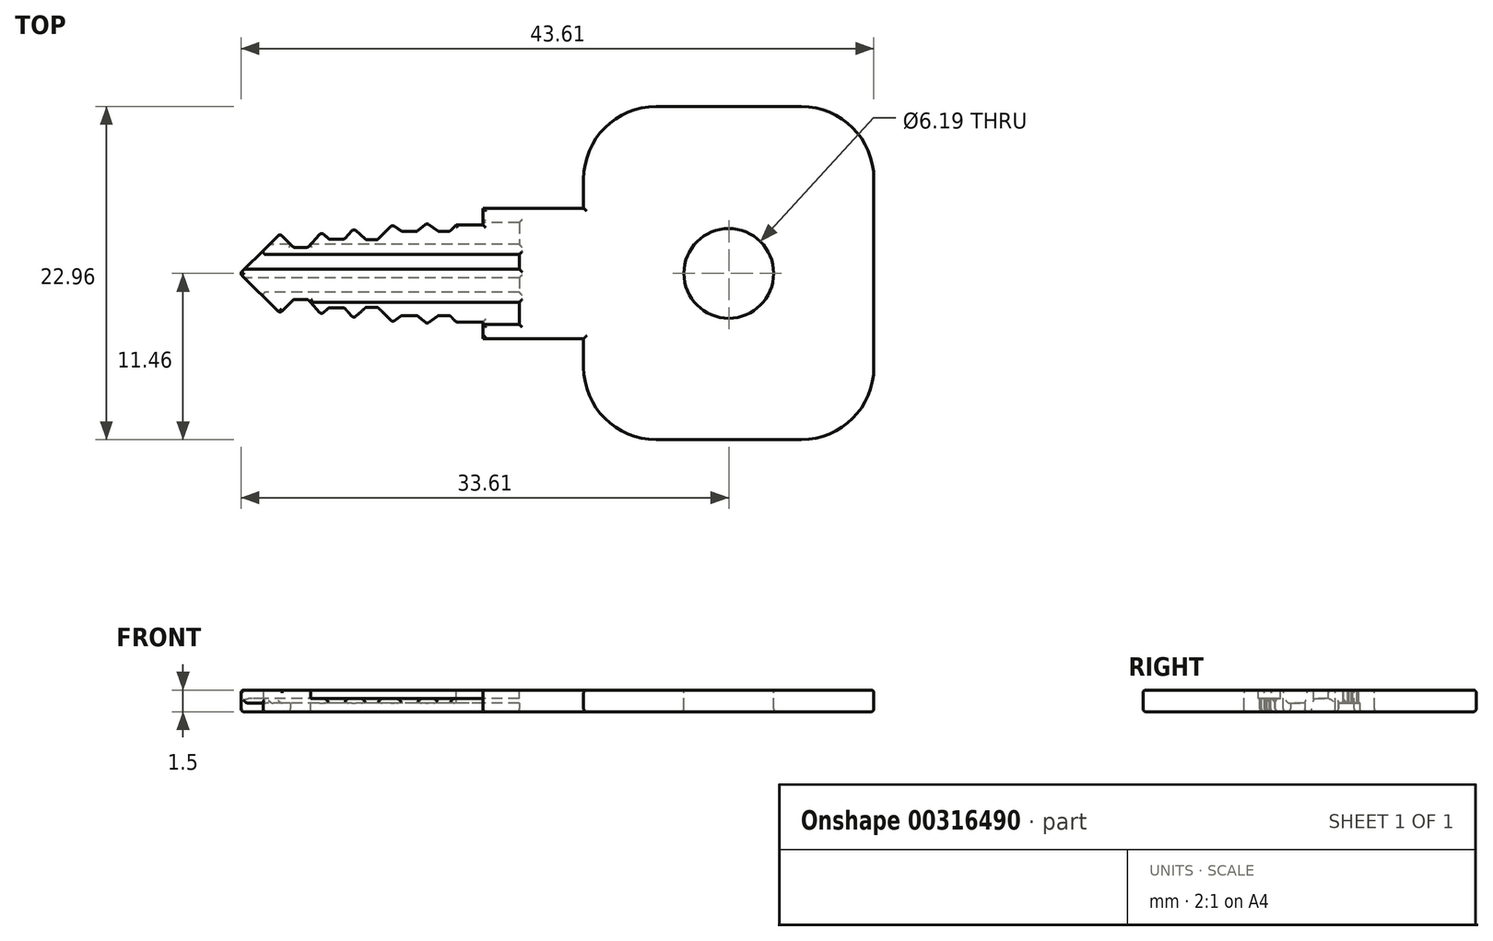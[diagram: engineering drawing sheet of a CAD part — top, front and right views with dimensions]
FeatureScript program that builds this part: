
annotation { "Feature Type Name" : "Feature", "Feature Type Description" : "" }
export const myFeature = defineFeature(function(context is Context, id is Id, definition is map)
    precondition{}
    {
        {
            var Q0;
            Q0=qCreatedBy(makeId("Right.planeOp"),FACE);
            var sketch = newSketch(context, id + "F0", { "sketchPlane" : qUnion([Q0])});
            skLineSegment(sketch, "E0.bottom", {"start": v(4.5, 0.75) * mm, "end": v(-4.5, 0.75) * mm});
            skLineSegment(sketch, "E0.top", {"start": v(4.5, -0.75) * mm, "end": v(-4.5, -0.75) * mm});
            skLineSegment(sketch, "E0.left", {"start": v(4.5, 0.75) * mm, "end": v(4.5, -0.75) * mm});
            skLineSegment(sketch, "E0.right", {"start": v(-4.5, 0.75) * mm, "end": v(-4.5, -0.75) * mm});
            skPoint(sketch, "E0.middle", {"position": v(0, 0) * mm});
            skSolve(sketch);
        }
        {
            var Q0;
            Q0 = qSketchRegion(id + "F0", true);
            extrude(context, id + "F1", {"entities" : qUnion([Q0]), "depth" : 25 * mm});
        }
        {
            var Q0;
            Q0=makeQuery(id+"F1.opExtrude","SWEPT_FACE",FACE,{"disambiguationData":[OSD([sQuery(id+"F0.wireOp",EDGE,"E0.bottom")])]});
            var sketch = newSketch(context, id + "F2", { "sketchPlane" : qUnion([Q0])});
            skLineSegment(sketch, "E1", {"start": v(0, 0) * mm, "end": v(0, -4.5) * mm});
            skLineSegment(sketch, "E2", {"start": v(18.06, -4.5) * mm, "end": v(18.06, -3.35) * mm});
            skLineSegment(sketch, "E3", {"start": v(18.06, -3.35) * mm, "end": v(16.22, -3.35) * mm});
            skLineSegment(sketch, "E4", {"start": v(16.22, -3.35) * mm, "end": v(15.77, -2.9) * mm});
            skLineSegment(sketch, "E5", {"start": v(15.77, -2.9) * mm, "end": v(14.99, -2.9) * mm});
            skLineSegment(sketch, "E6", {"start": v(14.99, -2.9) * mm, "end": v(14.2, -3.47) * mm});
            skLineSegment(sketch, "E7", {"start": v(14.2, -3.47) * mm, "end": v(13.51, -2.9) * mm});
            skLineSegment(sketch, "E8", {"start": v(13.51, -2.9) * mm, "end": v(12.47, -2.9) * mm});
            skLineSegment(sketch, "E9", {"start": v(12.47, -2.9) * mm, "end": v(11.83, -3.35) * mm});
            skLineSegment(sketch, "E10", {"start": v(11.83, -3.35) * mm, "end": v(10.8, -2.33) * mm});
            skLineSegment(sketch, "E11", {"start": v(10.8, -2.33) * mm, "end": v(10, -2.33) * mm});
            skLineSegment(sketch, "E12", {"start": v(10, -2.33) * mm, "end": v(9.16, -3.1) * mm});
            skLineSegment(sketch, "E13", {"start": v(9.16, -3.1) * mm, "end": v(8.5, -2.36) * mm});
            skLineSegment(sketch, "E14", {"start": v(8.5, -2.36) * mm, "end": v(7.45, -2.36) * mm});
            skLineSegment(sketch, "E15", {"start": v(7.45, -2.36) * mm, "end": v(6.93, -2.83) * mm});
            skLineSegment(sketch, "E16", {"start": v(6.93, -2.83) * mm, "end": v(6, -1.8) * mm});
            skLineSegment(sketch, "E17", {"start": v(6, -1.8) * mm, "end": v(5, -1.8) * mm});
            skLineSegment(sketch, "E18", {"start": v(5, -1.8) * mm, "end": v(4.07, -2.73) * mm});
            skLineSegment(sketch, "E19", {"start": v(4.07, -2.73) * mm, "end": v(1.3, 0) * mm});
            skLineSegment(sketch, "E20", {"start": v(1.3, 0) * mm, "end": v(0, 0) * mm});
            skLineSegment(sketch, "E21.MirrorCS", {"start": v(14.2, 3.47) * mm, "end": v(13.51, 2.9) * mm});
            skLineSegment(sketch, "E22.MirrorCS", {"start": v(10.8, 2.33) * mm, "end": v(10, 2.33) * mm});
            skLineSegment(sketch, "E23.MirrorCS", {"start": v(16.22, 3.35) * mm, "end": v(15.77, 2.9) * mm});
            skLineSegment(sketch, "E24.MirrorCS", {"start": v(15.77, 2.9) * mm, "end": v(14.99, 2.9) * mm});
            skLineSegment(sketch, "E25.MirrorCS", {"start": v(7.45, 2.36) * mm, "end": v(6.93, 2.83) * mm});
            skLineSegment(sketch, "E26.MirrorCS", {"start": v(12.47, 2.9) * mm, "end": v(11.83, 3.35) * mm});
            skLineSegment(sketch, "E27.MirrorCS", {"start": v(14.99, 2.9) * mm, "end": v(14.2, 3.47) * mm});
            skLineSegment(sketch, "E28.MirrorCS", {"start": v(0, 0) * mm, "end": v(0, 4.5) * mm});
            skLineSegment(sketch, "E29.MirrorCS", {"start": v(18.06, 4.5) * mm, "end": v(18.06, 3.35) * mm});
            skLineSegment(sketch, "E30.MirrorCS", {"start": v(6, 1.8) * mm, "end": v(5, 1.8) * mm});
            skLineSegment(sketch, "E31.MirrorCS", {"start": v(18.06, 3.35) * mm, "end": v(16.22, 3.35) * mm});
            skLineSegment(sketch, "E32.MirrorCS", {"start": v(9.16, 3.1) * mm, "end": v(8.5, 2.36) * mm});
            skLineSegment(sketch, "E33.MirrorCS", {"start": v(5, 1.8) * mm, "end": v(4.07, 2.73) * mm});
            skLineSegment(sketch, "E34.MirrorCS", {"start": v(13.51, 2.9) * mm, "end": v(12.47, 2.9) * mm});
            skLineSegment(sketch, "E35.MirrorCS", {"start": v(4.07, 2.73) * mm, "end": v(1.3, 0) * mm});
            skLineSegment(sketch, "E36.MirrorCS", {"start": v(8.5, 2.36) * mm, "end": v(7.45, 2.36) * mm});
            skLineSegment(sketch, "E37.MirrorCS", {"start": v(11.83, 3.35) * mm, "end": v(10.8, 2.33) * mm});
            skLineSegment(sketch, "E38.MirrorCS", {"start": v(6.93, 2.83) * mm, "end": v(6, 1.8) * mm});
            skLineSegment(sketch, "E39.MirrorCS", {"start": v(10, 2.33) * mm, "end": v(9.16, 3.1) * mm});
            skSolve(sketch);
        }
        {
            var Q0;
            {var subQ0=sQuery(id+"F2.wireOp",EDGE,"E1");Q0=makeQuery(id+"F2.imprint","IMPRINT",FACE,{"disambiguationData":[TD([[makeQuery(id+"F2.imprint","IMPRINT",EDGE,{"derivedFrom":subQ0}),1.0]])]});}
            var Q1;
            Q1=makeQuery(id+"F2.imprint","IMPRINT",FACE,{"disambiguationData":[TD([[makeQuery(id+"F2.imprint","IMPRINT",EDGE,{"derivedFrom":sQuery(id+"F2.wireOp",EDGE,"E21.MirrorCS")}),-1.0]])]});
            extrude(context, id + "F3", {"entities" : qUnion([Q0, Q1]), "operationType" : NewBodyOperationType.REMOVE, "oppositeDirection" : true, "depth" : 25 * mm});
        }
        {
            var Q0;
            Q0=makeQuery(id+"F1.opExtrude","SWEPT_FACE",FACE,{"disambiguationData":[OSD([sQuery(id+"F0.wireOp",EDGE,"E0.bottom")])]});
            var sketch = newSketch(context, id + "F4", { "sketchPlane" : qUnion([Q0])});
            skLineSegment(sketch, "E40.bottom", {"start": v(20.56, -3.5) * mm, "end": v(-1.2, -3.5) * mm});
            skLineSegment(sketch, "E40.top", {"start": v(20.56, -2) * mm, "end": v(-1.2, -2) * mm});
            skLineSegment(sketch, "E40.left", {"start": v(20.56, -3.5) * mm, "end": v(20.56, -2) * mm});
            skLineSegment(sketch, "E40.right", {"start": v(-1.2, -3.5) * mm, "end": v(-1.2, -2) * mm});
            skLineSegment(sketch, "E41.bottom", {"start": v(20.56, 0.3) * mm, "end": v(-1.1, 0.3) * mm});
            skLineSegment(sketch, "E41.top", {"start": v(20.56, 1.3) * mm, "end": v(-1.1, 1.3) * mm});
            skLineSegment(sketch, "E41.left", {"start": v(20.56, 0.3) * mm, "end": v(20.56, 1.3) * mm});
            skLineSegment(sketch, "E41.right", {"start": v(-1.1, 0.3) * mm, "end": v(-1.1, 1.3) * mm});
            skSolve(sketch);
        }
        {
            var Q0;
            {var subQ0=sQuery(id+"F4.wireOp",EDGE,"E41.left");Q0=makeQuery(id+"F4.imprint","IMPRINT",FACE,{"disambiguationData":[TD([[makeQuery(id+"F4.imprint","IMPRINT",EDGE,{"derivedFrom":subQ0}),1.0]])]});}
            var Q1;
            {var subQ0=sQuery(id+"F4.wireOp",EDGE,"E40.left");Q1=makeQuery(id+"F4.imprint","IMPRINT",FACE,{"disambiguationData":[TD([[makeQuery(id+"F4.imprint","IMPRINT",EDGE,{"derivedFrom":subQ0}),1.0]])]});}
            var Q2;
            {var subQ0=sQuery(id+"F4.wireOp",EDGE,"E40.top");var subQ1=makeQuery(id+"F3.boolean.opBoolean","COPY",EDGE,{"derivedFrom":makeQuery(id+"F3.opExtrude","CAP_EDGE",EDGE,{"disambiguationData":[OSD([sQuery(id+"F2.wireOp",EDGE,"E19")])],"isStart":true})});var subQ2=makeQuery(id+"F4.imprint","INTERSECT",VERTEX,{"derivedFrom":[subQ1,subQ0]});Q2=makeQuery(id+"F4.imprint","IMPRINT",FACE,{"disambiguationData":[TD([[makeQuery(id+"F4.imprint","IMPRINT",EDGE,{"disambiguationData":[TD([[subQ2,1.0]])],"derivedFrom":subQ0}),1.0]])]});}
            extrude(context, id + "F5", {"entities" : qUnion([Q0, Q1, Q2]), "operationType" : NewBodyOperationType.REMOVE, "oppositeDirection" : true, "depth" : 0.6 * mm});
        }
        {
            var Q0;
            Q0=makeQuery(id+"F1.opExtrude","SWEPT_FACE",FACE,{"disambiguationData":[OSD([sQuery(id+"F0.wireOp",EDGE,"E0.top")])]});
            var sketch = newSketch(context, id + "F6", { "sketchPlane" : qUnion([Q0])});
            skLineSegment(sketch, "E42.bottom", {"start": v(20.56, -3.5) * mm, "end": v(-6.94, -3.5) * mm});
            skLineSegment(sketch, "E42.top", {"start": v(20.56, -2) * mm, "end": v(-6.94, -2) * mm});
            skLineSegment(sketch, "E42.left", {"start": v(20.56, -3.5) * mm, "end": v(20.56, -2) * mm});
            skLineSegment(sketch, "E42.right", {"start": v(-6.94, -3.5) * mm, "end": v(-6.94, -2) * mm});
            skLineSegment(sketch, "E43.bottom", {"start": v(20.56, 0.3) * mm, "end": v(-9.24, 0.3) * mm});
            skLineSegment(sketch, "E43.top", {"start": v(20.56, 1.3) * mm, "end": v(-9.24, 1.3) * mm});
            skLineSegment(sketch, "E43.left", {"start": v(20.56, 0.3) * mm, "end": v(20.56, 1.3) * mm});
            skLineSegment(sketch, "E43.right", {"start": v(-9.24, 0.3) * mm, "end": v(-9.24, 1.3) * mm});
            skSolve(sketch);
        }
        {
            var Q0;
            Q0 = qSketchRegion(id + "F6", true);
            extrude(context, id + "F7", {"entities" : qUnion([Q0]), "operationType" : NewBodyOperationType.REMOVE, "oppositeDirection" : true, "depth" : 0.6 * mm});
        }
        {
            var Q0;
            Q0=makeQuery(id+"F1.opExtrude","CAP_FACE",FACE,{"disambiguationData":[OSD([sQuery(id+"F0.wireOp",EDGE,"E0.bottom"),sQuery(id+"F0.wireOp",EDGE,"E0.top"),sQuery(id+"F0.wireOp",EDGE,"E0.left"),sQuery(id+"F0.wireOp",EDGE,"E0.right")])],"isStart":false});
            var sketch = newSketch(context, id + "F8", { "sketchPlane" : qUnion([Q0])});
            skPoint(sketch, "E44.firstSnap0", {"position": v(0, 0.75) * mm});
            skLineSegment(sketch, "E44.bottom", {"start": v(11.5, 0.75) * mm, "end": v(-11.46, 0.75) * mm});
            skLineSegment(sketch, "E44.top", {"start": v(11.5, -0.75) * mm, "end": v(-11.46, -0.75) * mm});
            skLineSegment(sketch, "E44.left", {"start": v(11.5, 0.75) * mm, "end": v(11.5, -0.75) * mm});
            skLineSegment(sketch, "E44.right", {"start": v(-11.46, 0.75) * mm, "end": v(-11.46, -0.75) * mm});
            skSolve(sketch);
        }
        {
            var Q0;
            Q0 = qSketchRegion(id + "F8", true);
            extrude(context, id + "F9", {"entities" : qUnion([Q0]), "operationType" : NewBodyOperationType.ADD, "depth" : 20 * mm});
        }
        {
            var Q0;
            Q0=makeQuery(id+"F9.boolean.opBoolean","MERGE",FACE,{"derivedFrom":[makeQuery(id+"F1.opExtrude","SWEPT_FACE",FACE,{"disambiguationData":[OSD([sQuery(id+"F0.wireOp",EDGE,"E0.bottom")])]}),makeQuery(id+"F9.opExtrude","SWEPT_FACE",FACE,{"disambiguationData":[OSD([sQuery(id+"F8.wireOp",EDGE,"E44.bottom")])]})]});
            var sketch = newSketch(context, id + "F10", { "sketchPlane" : qUnion([Q0])});
            skCircle(sketch, "E45", {"center": v(35, 0) * mm, "radius": 3.1 * mm});
            skPoint(sketch, "E45.centerSnap0", {"position": v(35, 11.5) * mm});
            skSolve(sketch);
        }
        {
            var Q0;
            Q0=makeQuery(id+"F10.imprint","IMPRINT",FACE,{"disambiguationData":[TD([[makeQuery(id+"F10.imprint","IMPRINT",EDGE,{"derivedFrom":sQuery(id+"F10.wireOp",EDGE,"E45")}),1.0]])]});
            extrude(context, id + "F11", {"entities" : qUnion([Q0]), "operationType" : NewBodyOperationType.REMOVE, "oppositeDirection" : true, "depth" : 25 * mm});
        }
        {
            var Q0;
            Q0=makeQuery(id+"F3.boolean.opBoolean","COPY",FACE,{"derivedFrom":makeQuery(id+"F3.opExtrude","SWEPT_FACE",FACE,{"disambiguationData":[OSD([sQuery(id+"F2.wireOp",EDGE,"E17")])]})});
            var Q1;
            Q1=makeQuery(id+"F3.boolean.opBoolean","COPY",FACE,{"derivedFrom":makeQuery(id+"F3.opExtrude","SWEPT_FACE",FACE,{"disambiguationData":[OSD([sQuery(id+"F2.wireOp",EDGE,"E18")])]})});
            var Q2;
            Q2=makeQuery(id+"F3.boolean.opBoolean","COPY",FACE,{"derivedFrom":makeQuery(id+"F3.opExtrude","SWEPT_FACE",FACE,{"disambiguationData":[OSD([sQuery(id+"F2.wireOp",EDGE,"E19")])]})});
            var Q3;
            Q3=makeQuery(id+"F3.boolean.opBoolean","COPY",FACE,{"derivedFrom":makeQuery(id+"F3.opExtrude","SWEPT_FACE",FACE,{"disambiguationData":[OSD([sQuery(id+"F2.wireOp",EDGE,"E14")])]})});
            var Q4;
            Q4=makeQuery(id+"F3.boolean.opBoolean","COPY",FACE,{"derivedFrom":makeQuery(id+"F3.opExtrude","SWEPT_FACE",FACE,{"disambiguationData":[OSD([sQuery(id+"F2.wireOp",EDGE,"E11")])]})});
            var Q5;
            Q5=makeQuery(id+"F3.boolean.opBoolean","COPY",FACE,{"derivedFrom":makeQuery(id+"F3.opExtrude","SWEPT_FACE",FACE,{"disambiguationData":[OSD([sQuery(id+"F2.wireOp",EDGE,"E8")])]})});
            var Q6;
            Q6=makeQuery(id+"F3.boolean.opBoolean","COPY",FACE,{"derivedFrom":makeQuery(id+"F3.opExtrude","SWEPT_FACE",FACE,{"disambiguationData":[OSD([sQuery(id+"F2.wireOp",EDGE,"E5")])]})});
            var Q7;
            Q7=makeQuery(id+"F3.boolean.opBoolean","COPY",EDGE,{"derivedFrom":makeQuery(id+"F3.opExtrude","SWEPT_EDGE",EDGE,{"disambiguationData":[OSD([sQuery(id+"F2.wireOp",EDGE,"E12"),sQuery(id+"F2.wireOp",EDGE,"E13")])]})});
            var Q8;
            Q8=makeQuery(id+"F3.boolean.opBoolean","COPY",EDGE,{"derivedFrom":makeQuery(id+"F3.opExtrude","SWEPT_EDGE",EDGE,{"disambiguationData":[OSD([sQuery(id+"F2.wireOp",EDGE,"E9"),sQuery(id+"F2.wireOp",EDGE,"E10")])]})});
            var Q9;
            Q9=makeQuery(id+"F3.boolean.opBoolean","COPY",EDGE,{"derivedFrom":makeQuery(id+"F3.opExtrude","SWEPT_EDGE",EDGE,{"disambiguationData":[OSD([sQuery(id+"F2.wireOp",EDGE,"E6"),sQuery(id+"F2.wireOp",EDGE,"E7")])]})});
            var Q10;
            Q10=makeQuery(id+"F3.boolean.opBoolean","COPY",EDGE,{"derivedFrom":makeQuery(id+"F3.opExtrude","SWEPT_EDGE",EDGE,{"disambiguationData":[OSD([sQuery(id+"F2.wireOp",EDGE,"E3"),sQuery(id+"F2.wireOp",EDGE,"E4")])]})});
            var Q11;
            Q11=makeQuery(id+"F3.boolean.opBoolean","COPY",EDGE,{"derivedFrom":makeQuery(id+"F3.opExtrude","SWEPT_EDGE",EDGE,{"disambiguationData":[OSD([sQuery(id+"F2.wireOp",EDGE,"E15"),sQuery(id+"F2.wireOp",EDGE,"E16")])]})});
            var Q12;
            Q12=makeQuery(id+"F3.boolean.opBoolean","COPY",FACE,{"derivedFrom":makeQuery(id+"F3.opExtrude","SWEPT_FACE",FACE,{"disambiguationData":[OSD([sQuery(id+"F2.wireOp",EDGE,"E35.MirrorCS")])]})});
            var Q13;
            Q13=makeQuery(id+"F3.boolean.opBoolean","COPY",FACE,{"derivedFrom":makeQuery(id+"F3.opExtrude","SWEPT_FACE",FACE,{"disambiguationData":[OSD([sQuery(id+"F2.wireOp",EDGE,"E30.MirrorCS")])]})});
            var Q14;
            Q14=makeQuery(id+"F3.boolean.opBoolean","COPY",FACE,{"derivedFrom":makeQuery(id+"F3.opExtrude","SWEPT_FACE",FACE,{"disambiguationData":[OSD([sQuery(id+"F2.wireOp",EDGE,"E36.MirrorCS")])]})});
            var Q15;
            Q15=makeQuery(id+"F3.boolean.opBoolean","COPY",FACE,{"derivedFrom":makeQuery(id+"F3.opExtrude","SWEPT_FACE",FACE,{"disambiguationData":[OSD([sQuery(id+"F2.wireOp",EDGE,"E22.MirrorCS")])]})});
            var Q16;
            Q16=makeQuery(id+"F3.boolean.opBoolean","COPY",FACE,{"derivedFrom":makeQuery(id+"F3.opExtrude","SWEPT_FACE",FACE,{"disambiguationData":[OSD([sQuery(id+"F2.wireOp",EDGE,"E34.MirrorCS")])]})});
            var Q17;
            Q17=makeQuery(id+"F3.boolean.opBoolean","COPY",FACE,{"derivedFrom":makeQuery(id+"F3.opExtrude","SWEPT_FACE",FACE,{"disambiguationData":[OSD([sQuery(id+"F2.wireOp",EDGE,"E24.MirrorCS")])]})});
            var Q18;
            Q18=makeQuery(id+"F3.boolean.opBoolean","COPY",EDGE,{"derivedFrom":makeQuery(id+"F3.opExtrude","SWEPT_EDGE",EDGE,{"disambiguationData":[OSD([sQuery(id+"F2.wireOp",EDGE,"E32.MirrorCS"),sQuery(id+"F2.wireOp",EDGE,"E39.MirrorCS")])]})});
            var Q19;
            Q19=makeQuery(id+"F3.boolean.opBoolean","COPY",EDGE,{"derivedFrom":makeQuery(id+"F3.opExtrude","SWEPT_EDGE",EDGE,{"disambiguationData":[OSD([sQuery(id+"F2.wireOp",EDGE,"E25.MirrorCS"),sQuery(id+"F2.wireOp",EDGE,"E38.MirrorCS")])]})});
            var Q20;
            Q20=makeQuery(id+"F3.boolean.opBoolean","COPY",EDGE,{"derivedFrom":makeQuery(id+"F3.opExtrude","SWEPT_EDGE",EDGE,{"disambiguationData":[OSD([sQuery(id+"F2.wireOp",EDGE,"E21.MirrorCS"),sQuery(id+"F2.wireOp",EDGE,"E27.MirrorCS")])]})});
            var Q21;
            Q21=makeQuery(id+"F3.boolean.opBoolean","COPY",EDGE,{"derivedFrom":makeQuery(id+"F3.opExtrude","SWEPT_EDGE",EDGE,{"disambiguationData":[OSD([sQuery(id+"F2.wireOp",EDGE,"E26.MirrorCS"),sQuery(id+"F2.wireOp",EDGE,"E37.MirrorCS")])]})});
            var Q22;
            Q22=makeQuery(id+"F9.boolean.opBoolean","MERGE",FACE,{"derivedFrom":[makeQuery(id+"F1.opExtrude","SWEPT_FACE",FACE,{"disambiguationData":[OSD([sQuery(id+"F0.wireOp",EDGE,"E0.bottom")])]}),makeQuery(id+"F9.opExtrude","SWEPT_FACE",FACE,{"disambiguationData":[OSD([sQuery(id+"F8.wireOp",EDGE,"E44.bottom")])]})]});
            var Q23;
            Q23=makeQuery(id+"F9.boolean.opBoolean","MERGE",FACE,{"derivedFrom":[makeQuery(id+"F1.opExtrude","SWEPT_FACE",FACE,{"disambiguationData":[OSD([sQuery(id+"F0.wireOp",EDGE,"E0.top")])]}),makeQuery(id+"F9.opExtrude","SWEPT_FACE",FACE,{"disambiguationData":[OSD([sQuery(id+"F8.wireOp",EDGE,"E44.top")])]})]});
            fillet(context, id + "F12", {"entities" : qUnion([Q0, Q1, Q2, Q3, Q4, Q5, Q6, Q7, Q8, Q9, Q10, Q11, Q12, Q13, Q14, Q15, Q16, Q17, Q18, Q19, Q20, Q21, Q22, Q23]), "radius" : 0.2 * mm, "tangentPropagation" : true, "allowEdgeOverflow" : false});
        }
        {
            var Q0;
            Q0=makeQuery(id+"F9.opExtrude","CAP_EDGE",EDGE,{"disambiguationData":[OSD([sQuery(id+"F8.wireOp",EDGE,"E44.left")])],"isStart":false});
            var Q1;
            Q1=makeQuery(id+"F9.opExtrude","CAP_EDGE",EDGE,{"disambiguationData":[OSD([sQuery(id+"F8.wireOp",EDGE,"E44.left")])],"isStart":true});
            var Q2;
            Q2=makeQuery(id+"F9.opExtrude","CAP_EDGE",EDGE,{"disambiguationData":[OSD([sQuery(id+"F8.wireOp",EDGE,"E44.right")])],"isStart":true});
            var Q3;
            Q3=makeQuery(id+"F9.opExtrude","CAP_EDGE",EDGE,{"disambiguationData":[OSD([sQuery(id+"F8.wireOp",EDGE,"E44.right")])],"isStart":false});
            fillet(context, id + "F13", {"entities" : qUnion([Q0, Q1, Q2, Q3]), "radius" : 5 * mm, "tangentPropagation" : true, "allowEdgeOverflow" : false});
        }
    });
